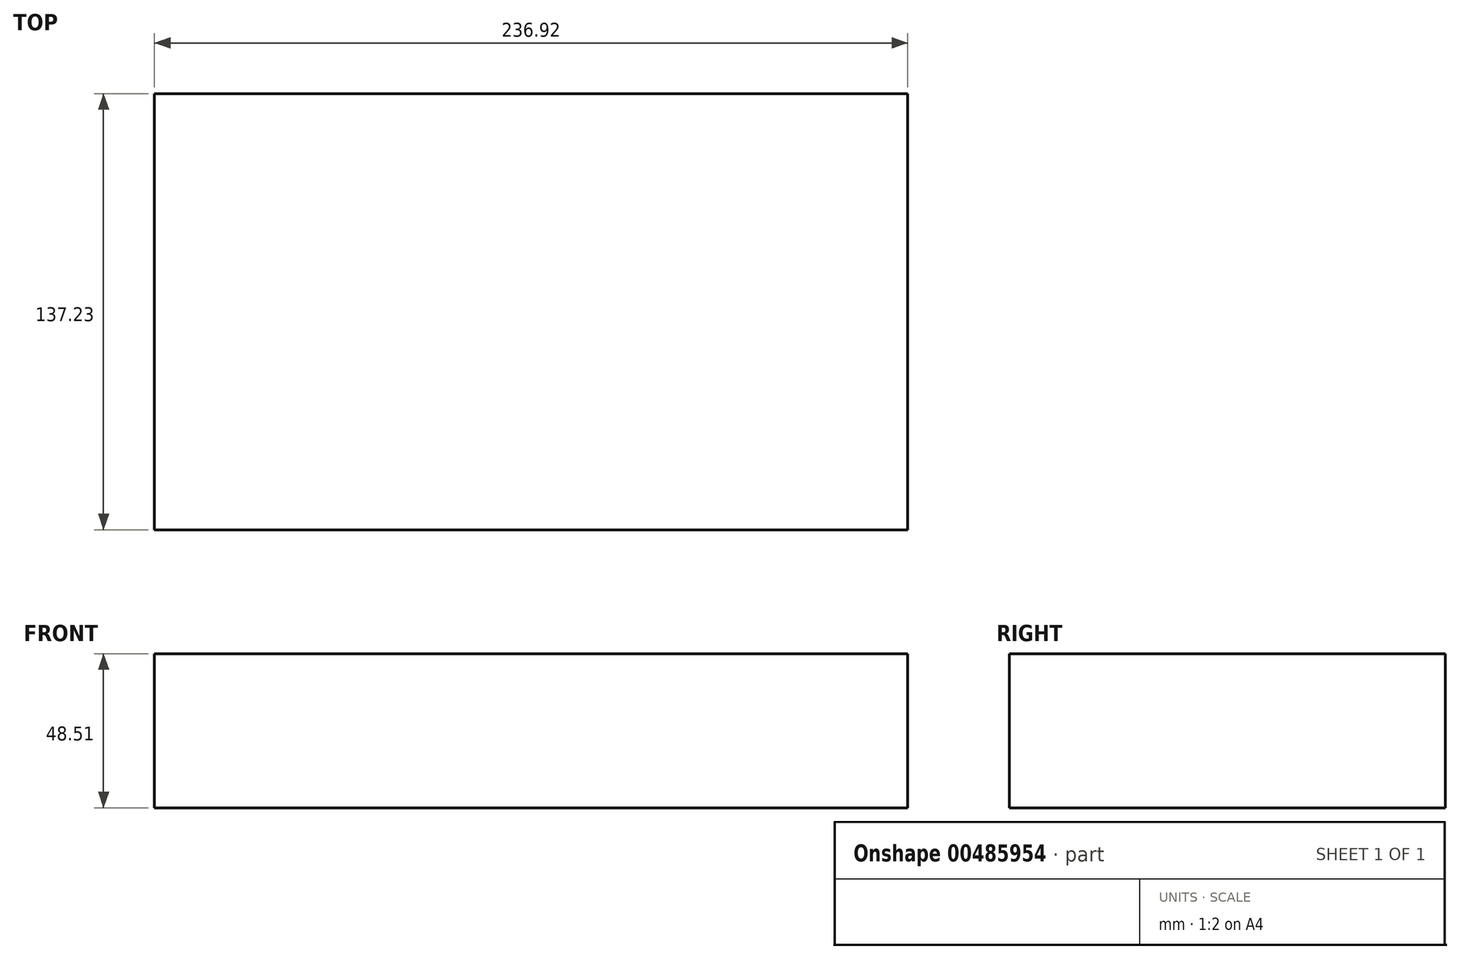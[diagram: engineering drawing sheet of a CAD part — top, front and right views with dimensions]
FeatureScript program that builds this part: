
annotation { "Feature Type Name" : "Feature", "Feature Type Description" : "" }
export const myFeature = defineFeature(function(context is Context, id is Id, definition is map)
    precondition{}
    {
        {
            var Q0;
            Q0=qCreatedBy(makeId("Top.planeOp"),FACE);
            var sketch = newSketch(context, id + "F0", { "sketchPlane" : qUnion([Q0])});
            skLineSegment(sketch, "E0.bottom", {"start": v(-134.98, 61.1) * mm, "end": v(101.94, 61.1) * mm});
            skLineSegment(sketch, "E0.top", {"start": v(-134.98, -76.12) * mm, "end": v(101.94, -76.12) * mm});
            skLineSegment(sketch, "E0.left", {"start": v(-134.98, 61.1) * mm, "end": v(-134.98, -76.12) * mm});
            skLineSegment(sketch, "E0.right", {"start": v(101.94, 61.1) * mm, "end": v(101.94, -76.12) * mm});
            skSolve(sketch);
        }
        {
            var Q0;
            Q0=makeQuery(id+"F0.imprint","IMPRINT",FACE,{"disambiguationData":[TD([[makeQuery(id+"F0.imprint","IMPRINT",EDGE,{"derivedFrom":sQuery(id+"F0.wireOp",EDGE,"E0.bottom")}),-1.0]])]});
            extrude(context, id + "F1", {"entities" : qUnion([Q0]), "depth" : 48.5 * mm});
        }
    });
